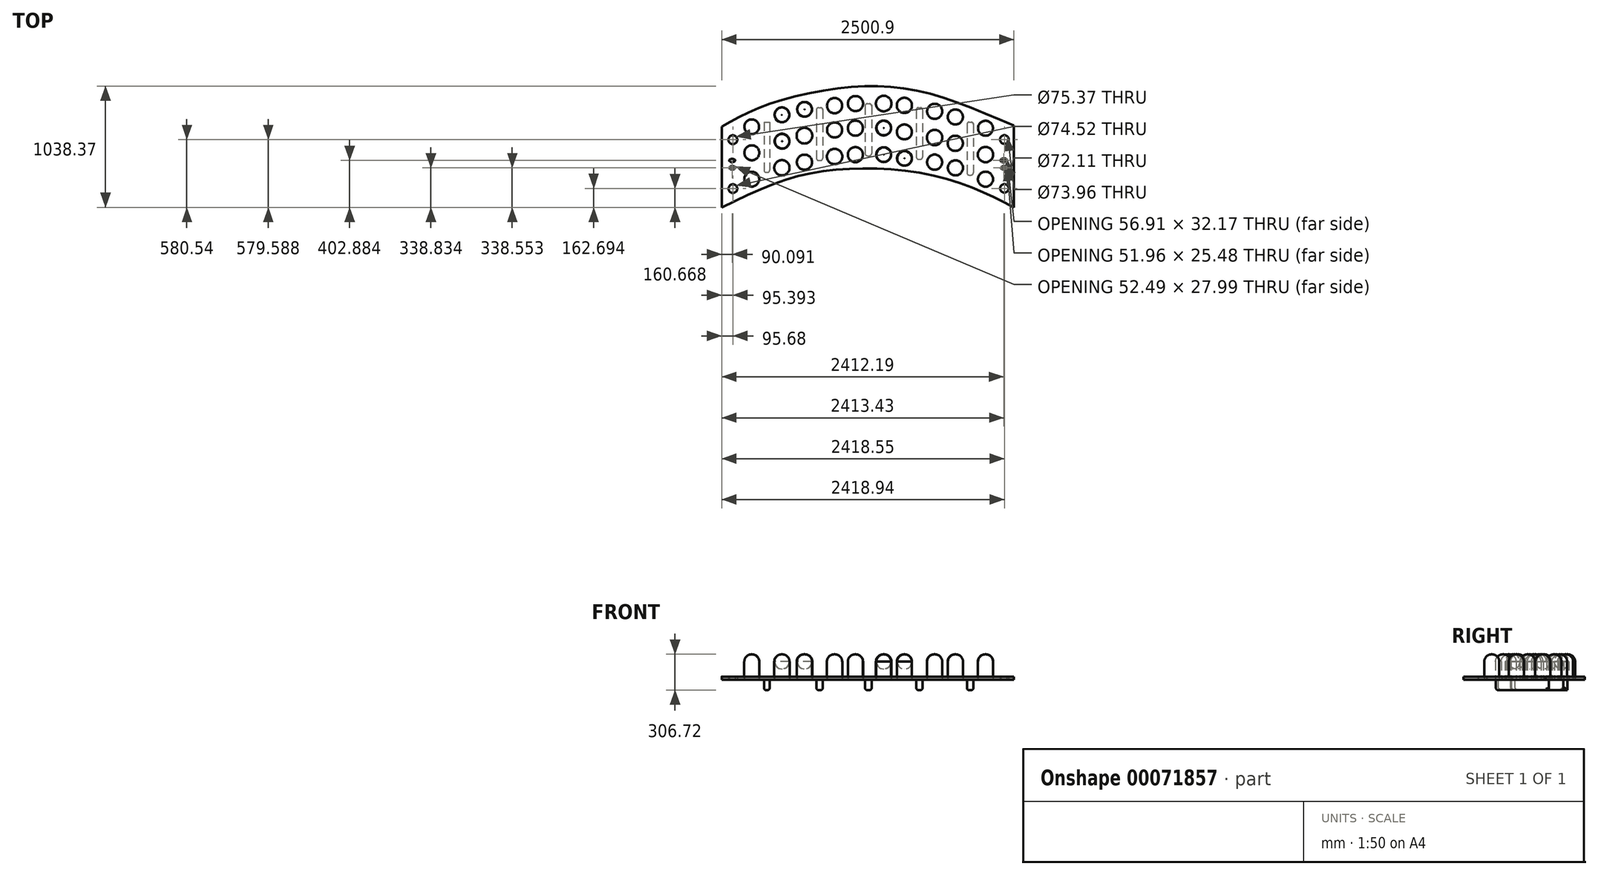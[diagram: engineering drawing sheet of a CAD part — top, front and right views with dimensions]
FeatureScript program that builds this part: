
annotation { "Feature Type Name" : "Feature", "Feature Type Description" : "" }
export const myFeature = defineFeature(function(context is Context, id is Id, definition is map)
    precondition{}
    {
        {
            var Q0;
            Q0=qCreatedBy(makeId("Top.planeOp"),FACE);
            var sketch = newSketch(context, id + "F0", { "sketchPlane" : qUnion([Q0])});
            skCircle(sketch, "E0", {"center": v(-1121.67, 314.92) * mm, "radius": 37.68 * mm});
            skArc(sketch, "E1", {"start": v(-1009.36, 266.44) * mm, "mid": v(-958.88, 121.92) * mm, "end": v(-910.93, 267.3) * mm});
            skFitSpline(sketch, "E2", {"points": [v(-1009.36, 266.44) * mm, v(-910.93, 267.3) * mm], "startDerivative": vector(98.35, 0.86) * mm, "endDerivative": vector(98.35, 0.86) * mm});
            skCircle(sketch, "E3", {"center": v(-959.59, 202.75) * mm, "radius": 63.82 * mm});
            skCircle(sketch, "E4", {"center": v(-1121.38, -104) * mm, "radius": 37.26 * mm});
            skCircle(sketch, "E5", {"center": v(1201.49, -101.98) * mm, "radius": 36.06 * mm});
            skCircle(sketch, "E6", {"center": v(1201.88, 315.87) * mm, "radius": 36.98 * mm});
            skCircle(sketch, "E7", {"center": v(1040.12, -23.25) * mm, "radius": 64.34 * mm});
            skArc(sketch, "E8", {"start": v(996.77, 45.5) * mm, "mid": v(1039.5, -104.53) * mm, "end": v(1084.49, 44.85) * mm});
            skArc(sketch, "E9", {"start": v(1084.6, 118.34) * mm, "mid": v(1039.83, 269.47) * mm, "end": v(996.09, 118.03) * mm});
            skCircle(sketch, "E10", {"center": v(1040.1, 187.36) * mm, "radius": 65.52 * mm});
            skCircle(sketch, "E11", {"center": v(782.85, 73.45) * mm, "radius": 64.5 * mm});
            skArc(sketch, "E12", {"start": v(739.54, 141.2) * mm, "mid": v(783.11, -6.96) * mm, "end": v(825.71, 141.49) * mm});
            skCircle(sketch, "E13", {"center": v(604.63, 122.55) * mm, "radius": 64.82 * mm});
            skArc(sketch, "E14", {"start": v(562.8, 190.06) * mm, "mid": v(605.03, 43.13) * mm, "end": v(645.78, 190.48) * mm});
            skCircle(sketch, "E15", {"center": v(781.42, 283.68) * mm, "radius": 65 * mm});
            skArc(sketch, "E16", {"start": v(735.27, 351.66) * mm, "mid": v(781.19, 201.51) * mm, "end": v(827.98, 351.39) * mm});
            skCircle(sketch, "E17", {"center": v(1040.05, 412.9) * mm, "radius": 64.08 * mm});
            skArc(sketch, "E18", {"start": v(1082.73, 344.5) * mm, "mid": v(1040.14, 493.54) * mm, "end": v(997.22, 344.6) * mm});
            skCircle(sketch, "E19", {"center": v(781.81, 509.34) * mm, "radius": 64.52 * mm});
            skArc(sketch, "E20", {"start": v(826.57, 440.73) * mm, "mid": v(781.74, 591.27) * mm, "end": v(737.18, 440.65) * mm});
            skCircle(sketch, "E21", {"center": v(605.1, 557.46) * mm, "radius": 64.57 * mm});
            skArc(sketch, "E22", {"start": v(646.48, 489.26) * mm, "mid": v(604.55, 637.22) * mm, "end": v(564.68, 488.7) * mm});
            skCircle(sketch, "E23", {"center": v(604.23, 332.64) * mm, "radius": 65.8 * mm});
            skArc(sketch, "E24", {"start": v(642.2, 263.79) * mm, "mid": v(602.61, 413.33) * mm, "end": v(565.81, 263.08) * mm});
            skCircle(sketch, "E25", {"center": v(345.86, 608.12) * mm, "radius": 64.94 * mm});
            skCircle(sketch, "E26", {"center": v(169, 623.72) * mm, "radius": 66.59 * mm});
            skArc(sketch, "E27", {"start": v(211.25, 553.01) * mm, "mid": v(169.2, 706.09) * mm, "end": v(126.42, 553.22) * mm});
            skArc(sketch, "E28", {"start": v(392.18, 538) * mm, "mid": v(344.45, 692.14) * mm, "end": v(301.92, 536.48) * mm});
            skCircle(sketch, "E29", {"center": v(345.86, 381.33) * mm, "radius": 63.88 * mm});
            skArc(sketch, "E30", {"start": v(300.08, 449.99) * mm, "mid": v(345.37, 298.81) * mm, "end": v(392.45, 449.44) * mm});
            skCircle(sketch, "E31", {"center": v(169, 414.62) * mm, "radius": 63.6 * mm});
            skArc(sketch, "E32", {"start": v(210.1, 344.64) * mm, "mid": v(168.9, 495.77) * mm, "end": v(128.1, 344.53) * mm});
            skCircle(sketch, "E33", {"center": v(169, 186.8) * mm, "radius": 63.46 * mm});
            skArc(sketch, "E34", {"start": v(126.98, 255.02) * mm, "mid": v(168.76, 106.66) * mm, "end": v(211.44, 254.76) * mm});
            skCircle(sketch, "E35", {"center": v(346.9, 155.58) * mm, "radius": 63.46 * mm});
            skArc(sketch, "E36", {"start": v(299.4, 224.7) * mm, "mid": v(345.11, 74.2) * mm, "end": v(393.54, 223.85) * mm});
            skCircle(sketch, "E37", {"center": v(-72.35, 623.72) * mm, "radius": 64.8 * mm});
            skArc(sketch, "E38", {"start": v(-31.79, 552.97) * mm, "mid": v(-71.26, 705.26) * mm, "end": v(-114.78, 554.08) * mm});
            skCircle(sketch, "E39", {"center": v(-251.28, 606.04) * mm, "radius": 65.03 * mm});
            skArc(sketch, "E40", {"start": v(-206.16, 538) * mm, "mid": v(-251.6, 689.58) * mm, "end": v(-295.85, 537.65) * mm});
            skCircle(sketch, "E41", {"center": v(-73.39, 413.58) * mm, "radius": 64.63 * mm});
            skArc(sketch, "E42", {"start": v(-117.78, 482.86) * mm, "mid": v(-73.02, 331.3) * mm, "end": v(-29.61, 483.26) * mm});
            skCircle(sketch, "E43", {"center": v(-251.28, 397.98) * mm, "radius": 64.7 * mm});
            skArc(sketch, "E44", {"start": v(-209.8, 327.74) * mm, "mid": v(-251.54, 479.54) * mm, "end": v(-292.3, 327.48) * mm});
            skCircle(sketch, "E45", {"center": v(-73.52, 186.84) * mm, "radius": 64.82 * mm});
            skArc(sketch, "E46", {"start": v(-113.86, 256.24) * mm, "mid": v(-72.98, 106.57) * mm, "end": v(-34.13, 256.78) * mm});
            skCircle(sketch, "E47", {"center": v(-251.54, 170.66) * mm, "radius": 65.86 * mm});
            skArc(sketch, "E48", {"start": v(-294.03, 239.99) * mm, "mid": v(-251.39, 89.35) * mm, "end": v(-209.32, 240.15) * mm});
            skCircle(sketch, "E49", {"center": v(-508.16, 574.52) * mm, "radius": 63.15 * mm});
            skArc(sketch, "E50", {"start": v(-459.73, 508.88) * mm, "mid": v(-509.28, 656.09) * mm, "end": v(-554.77, 507.58) * mm});
            skCircle(sketch, "E51", {"center": v(-509.33, 349.16) * mm, "radius": 67.21 * mm});
            skArc(sketch, "E52", {"start": v(-550.67, 417.2) * mm, "mid": v(-508.63, 269.54) * mm, "end": v(-469.18, 417.91) * mm});
            skCircle(sketch, "E53", {"center": v(-702, 527.82) * mm, "radius": 63.06 * mm});
            skArc(sketch, "E54", {"start": v(-653.72, 461.86) * mm, "mid": v(-702.05, 609.55) * mm, "end": v(-750.2, 461.8) * mm});
            skCircle(sketch, "E55", {"center": v(-700.83, 301.28) * mm, "radius": 63.74 * mm});
            skArc(sketch, "E56", {"start": v(-662.8, 232.28) * mm, "mid": v(-700.48, 380.06) * mm, "end": v(-739.47, 232.63) * mm});
            skCircle(sketch, "E57", {"center": v(-508.93, 122.36) * mm, "radius": 64.67 * mm});
            skArc(sketch, "E58", {"start": v(-554.53, 190.63) * mm, "mid": v(-508.86, 40.26) * mm, "end": v(-463.45, 190.7) * mm});
            skCircle(sketch, "E59", {"center": v(-702.18, 74.48) * mm, "radius": 65.4 * mm});
            skArc(sketch, "E60", {"start": v(-745.47, 142.47) * mm, "mid": v(-702.86, -6.12) * mm, "end": v(-657.77, 141.74) * mm});
            skCircle(sketch, "E61", {"center": v(-960.27, 425.7) * mm, "radius": 62.75 * mm});
            skArc(sketch, "E62", {"start": v(-914.27, 360.84) * mm, "mid": v(-957.9, 507.67) * mm, "end": v(-1003.02, 361.3) * mm});
            skCircle(sketch, "E63", {"center": v(-960.27, -23.05) * mm, "radius": 64.01 * mm});
            skArc(sketch, "E64", {"start": v(-1009.36, 44.48) * mm, "mid": v(-962.23, -105.4) * mm, "end": v(-915.1, 44.48) * mm});
            skFitSpline(sketch, "E65", {"points": [v(-1003.02, 361.3) * mm, v(-914.27, 360.84) * mm], "startDerivative": vector(88.69, -0.44) * mm, "endDerivative": vector(88.69, -0.44) * mm});
            skFitSpline(sketch, "E66", {"points": [v(-1009.36, 44.48) * mm, v(-915.1, 44.48) * mm], "startDerivative": vector(94.27, 0) * mm, "endDerivative": vector(94.27, 0) * mm});
            skFitSpline(sketch, "E67", {"points": [v(-745.47, 142.47) * mm, v(-657.77, 141.74) * mm], "startDerivative": vector(87.63, -0.72) * mm, "endDerivative": vector(87.63, -0.72) * mm});
            skFitSpline(sketch, "E68", {"points": [v(-739.47, 232.63) * mm, v(-662.8, 232.28) * mm], "startDerivative": vector(76.67, -0.26) * mm, "endDerivative": vector(76.67, -0.26) * mm});
            skFitSpline(sketch, "E69", {"points": [v(-750.2, 461.8) * mm, v(-653.72, 461.86) * mm], "startDerivative": vector(96.42, 0.06) * mm, "endDerivative": vector(96.42, 0.06) * mm});
            skFitSpline(sketch, "E70", {"points": [v(-554.53, 190.63) * mm, v(-463.45, 190.7) * mm], "startDerivative": vector(91.01, 0.07) * mm, "endDerivative": vector(91.01, 0.07) * mm});
            skFitSpline(sketch, "E71", {"points": [v(-550.67, 417.2) * mm, v(-469.18, 417.91) * mm], "startDerivative": vector(81.45, 0.75) * mm, "endDerivative": vector(81.45, 0.75) * mm});
            skFitSpline(sketch, "E72", {"points": [v(-554.77, 507.58) * mm, v(-459.73, 508.88) * mm], "startDerivative": vector(95, 1.36) * mm, "endDerivative": vector(95, 1.36) * mm});
            skFitSpline(sketch, "E73", {"points": [v(-295.85, 537.65) * mm, v(-206.16, 538) * mm], "startDerivative": vector(89.6, 0.34) * mm, "endDerivative": vector(89.6, 0.34) * mm});
            skFitSpline(sketch, "E74", {"points": [v(-292.3, 327.48) * mm, v(-209.8, 327.74) * mm], "startDerivative": vector(82.52, 0.22) * mm, "endDerivative": vector(82.52, 0.22) * mm});
            skFitSpline(sketch, "E75", {"points": [v(-294.03, 239.99) * mm, v(-209.32, 240.15) * mm], "startDerivative": vector(84.65, 0.17) * mm, "endDerivative": vector(84.65, 0.17) * mm});
            skFitSpline(sketch, "E76", {"points": [v(-31.79, 552.97) * mm, v(-114.78, 554.08) * mm], "startDerivative": vector(-82.96, 1.17) * mm, "endDerivative": vector(-82.96, 1.17) * mm});
            skFitSpline(sketch, "E77", {"points": [v(-29.61, 483.26) * mm, v(-117.78, 482.86) * mm], "startDerivative": vector(-88.09, -0.4) * mm, "endDerivative": vector(-88.09, -0.4) * mm});
            skFitSpline(sketch, "E78", {"points": [v(-34.13, 256.78) * mm, v(-113.86, 256.24) * mm], "startDerivative": vector(-79.72, -0.52) * mm, "endDerivative": vector(-79.72, -0.52) * mm});
            skFitSpline(sketch, "E79", {"points": [v(126.42, 553.22) * mm, v(211.25, 553.01) * mm], "startDerivative": vector(84.78, -0.22) * mm, "endDerivative": vector(84.78, -0.22) * mm});
            skFitSpline(sketch, "E80", {"points": [v(301.92, 536.48) * mm, v(392.18, 538) * mm], "startDerivative": vector(90.18, 1.52) * mm, "endDerivative": vector(90.18, 1.52) * mm});
            skFitSpline(sketch, "E81", {"points": [v(300.08, 449.99) * mm, v(392.45, 449.44) * mm], "startDerivative": vector(92.32, -0.53) * mm, "endDerivative": vector(92.32, -0.53) * mm});
            skFitSpline(sketch, "E82", {"points": [v(210.1, 344.64) * mm, v(128.1, 344.53) * mm], "startDerivative": vector(-81.99, -0.14) * mm, "endDerivative": vector(-81.99, -0.14) * mm});
            skFitSpline(sketch, "E83", {"points": [v(126.98, 255.02) * mm, v(211.44, 254.76) * mm], "startDerivative": vector(84.39, -0.26) * mm, "endDerivative": vector(84.39, -0.26) * mm});
            skFitSpline(sketch, "E84", {"points": [v(299.4, 224.7) * mm, v(393.54, 223.85) * mm], "startDerivative": vector(94.13, -0.8) * mm, "endDerivative": vector(94.13, -0.8) * mm});
            skFitSpline(sketch, "E85", {"points": [v(564.68, 488.7) * mm, v(646.48, 489.26) * mm], "startDerivative": vector(81.76, 0.6) * mm, "endDerivative": vector(81.76, 0.6) * mm});
            skFitSpline(sketch, "E86", {"points": [v(737.18, 440.65) * mm, v(826.57, 440.73) * mm], "startDerivative": vector(89.3, 0.08) * mm, "endDerivative": vector(89.3, 0.08) * mm});
            skFitSpline(sketch, "E87", {"points": [v(735.27, 351.66) * mm, v(827.98, 351.39) * mm], "startDerivative": vector(92.7, -0.2) * mm, "endDerivative": vector(92.7, -0.2) * mm});
            skFitSpline(sketch, "E88", {"points": [v(565.81, 263.08) * mm, v(642.2, 263.79) * mm], "startDerivative": vector(76.34, 0.69) * mm, "endDerivative": vector(76.34, 0.69) * mm});
            skFitSpline(sketch, "E89", {"points": [v(562.8, 190.06) * mm, v(645.78, 190.48) * mm], "startDerivative": vector(82.93, 0.43) * mm, "endDerivative": vector(82.93, 0.43) * mm});
            skFitSpline(sketch, "E90", {"points": [v(825.71, 141.49) * mm, v(739.54, 141.2) * mm], "startDerivative": vector(-86.1, -0.28) * mm, "endDerivative": vector(-86.1, -0.28) * mm});
            skFitSpline(sketch, "E91", {"points": [v(997.22, 344.6) * mm, v(1082.73, 344.5) * mm], "startDerivative": vector(85.43, -0.1) * mm, "endDerivative": vector(85.43, -0.1) * mm});
            skFitSpline(sketch, "E92", {"points": [v(996.09, 118.03) * mm, v(1084.6, 118.34) * mm], "startDerivative": vector(88.43, 0.3) * mm, "endDerivative": vector(88.43, 0.3) * mm});
            skFitSpline(sketch, "E93", {"points": [v(996.77, 45.5) * mm, v(1084.49, 44.85) * mm], "startDerivative": vector(87.64, -0.65) * mm, "endDerivative": vector(87.64, -0.65) * mm});
            skLineSegment(sketch, "E94.bottom", {"start": v(-855.95, 463.96) * mm, "end": v(-806.83, 463.96) * mm});
            skLineSegment(sketch, "E94.top", {"start": v(-855.95, 34.85) * mm, "end": v(-806.83, 34.85) * mm});
            skLineSegment(sketch, "E94.left", {"start": v(-855.95, 463.96) * mm, "end": v(-855.95, 34.85) * mm});
            skLineSegment(sketch, "E94.right", {"start": v(-806.83, 463.96) * mm, "end": v(-806.83, 34.85) * mm});
            skLineSegment(sketch, "E95.bottom", {"start": v(-407.37, 589.08) * mm, "end": v(-352.7, 589.08) * mm});
            skLineSegment(sketch, "E95.top", {"start": v(-407.37, 136.8) * mm, "end": v(-352.7, 136.8) * mm});
            skLineSegment(sketch, "E95.left", {"start": v(-407.37, 589.08) * mm, "end": v(-407.37, 136.8) * mm});
            skLineSegment(sketch, "E95.right", {"start": v(-352.7, 589.08) * mm, "end": v(-352.7, 136.8) * mm});
            skLineSegment(sketch, "E96.bottom", {"start": v(9.2, 622.77) * mm, "end": v(65.98, 622.77) * mm});
            skLineSegment(sketch, "E96.top", {"start": v(9.2, 177.29) * mm, "end": v(65.98, 177.29) * mm});
            skLineSegment(sketch, "E96.left", {"start": v(9.2, 622.77) * mm, "end": v(9.2, 177.29) * mm});
            skLineSegment(sketch, "E96.right", {"start": v(65.98, 622.77) * mm, "end": v(65.98, 177.29) * mm});
            skLineSegment(sketch, "E97.bottom", {"start": v(447.86, 589.71) * mm, "end": v(502.02, 589.71) * mm});
            skLineSegment(sketch, "E97.top", {"start": v(447.86, 146.74) * mm, "end": v(502.02, 146.74) * mm});
            skLineSegment(sketch, "E97.left", {"start": v(447.86, 589.71) * mm, "end": v(447.86, 146.74) * mm});
            skLineSegment(sketch, "E97.right", {"start": v(502.02, 589.71) * mm, "end": v(502.02, 146.74) * mm});
            skLineSegment(sketch, "E98.bottom", {"start": v(880.9, 464.82) * mm, "end": v(936.57, 464.82) * mm});
            skLineSegment(sketch, "E98.top", {"start": v(880.9, 12.03) * mm, "end": v(936.57, 12.03) * mm});
            skLineSegment(sketch, "E98.left", {"start": v(880.9, 464.82) * mm, "end": v(880.9, 12.03) * mm});
            skLineSegment(sketch, "E98.right", {"start": v(936.57, 464.82) * mm, "end": v(936.57, 12.03) * mm});
            skEllipse(sketch, "E99", {"center": v(1195.13, 138.21) * mm, "majorRadius": 28.45 * mm, "minorRadius": 16.08 * mm, "majorAxis": v(1, 0)});
            skEllipse(sketch, "E100", {"center": v(1196.37, 73.88) * mm, "majorRadius": 25.98 * mm, "minorRadius": 12.74 * mm, "majorAxis": v(1, 0)});
            skEllipse(sketch, "E101", {"center": v(-1127.84, 137.15) * mm, "majorRadius": 24.5 * mm, "minorRadius": 14.14 * mm, "majorAxis": v(-1, 0)});
            skEllipse(sketch, "E102", {"center": v(-1126.97, 74.16) * mm, "majorRadius": 26.24 * mm, "minorRadius": 14 * mm, "majorAxis": v(1, 0)});
            skFitSpline(sketch, "E103", {"points": [v(-1217.06, 426.7) * mm, v(-1216.3, -264.67) * mm], "startDerivative": vector(0, -694.41) * mm, "endDerivative": vector(0, -694.41) * mm});
            skFitSpline(sketch, "E104", {"points": [v(1283.84, -264.67) * mm, v(1283.84, 435.53) * mm], "startDerivative": vector(0, 703.24) * mm, "endDerivative": vector(0, 703.24) * mm});
            skPoint(sketch, "E105.3.internal.snap0", {"position": v(-702.05, 609.55) * mm});
            skFitSpline(sketch, "E105", {"points": [v(1283.84, 435.53) * mm, v(501.33, 723.9) * mm, v(-146, 762.14) * mm, v(-840.42, 609.55) * mm, v(-1217.06, 426.7) * mm], "startDerivative": vector(-2819.24, 1209.08) * mm, "endDerivative": vector(-1679, -949.55) * mm});
            skPoint(sketch, "E106.2.internal.snap0", {"position": v(-1126.97, 60.17) * mm});
            skFitSpline(sketch, "E106", {"points": [v(-1216.3, -264.67) * mm, v(-682.25, -32.14) * mm, v(-202.55, 60.17) * mm, v(371.33, 48.06) * mm, v(916.46, -90.83) * mm, v(1283.84, -264.67) * mm], "startDerivative": vector(2555.4, 1244.06) * mm, "endDerivative": vector(1956.51, -1028.42) * mm});
            skSolve(sketch);
        }
        {
            var Q0;
            Q0=makeQuery(id+"F0.imprint","IMPRINT",FACE,{"disambiguationData":[TD([[makeQuery(id+"F0.imprint","IMPRINT",EDGE,{"derivedFrom":sQuery(id+"F0.wireOp",EDGE,"E63")}),1.0]])]});
            var Q1;
            Q1=makeQuery(id+"F0.imprint","IMPRINT",FACE,{"disambiguationData":[TD([[makeQuery(id+"F0.imprint","IMPRINT",EDGE,{"derivedFrom":sQuery(id+"F0.wireOp",EDGE,"E3")}),1.0]])]});
            var Q2;
            Q2=makeQuery(id+"F0.imprint","IMPRINT",FACE,{"disambiguationData":[TD([[makeQuery(id+"F0.imprint","IMPRINT",EDGE,{"derivedFrom":sQuery(id+"F0.wireOp",EDGE,"E61")}),1.0]])]});
            var Q3;
            Q3=makeQuery(id+"F0.imprint","IMPRINT",FACE,{"disambiguationData":[TD([[makeQuery(id+"F0.imprint","IMPRINT",EDGE,{"derivedFrom":sQuery(id+"F0.wireOp",EDGE,"E53")}),1.0]])]});
            var Q4;
            Q4=makeQuery(id+"F0.imprint","IMPRINT",FACE,{"disambiguationData":[TD([[makeQuery(id+"F0.imprint","IMPRINT",EDGE,{"derivedFrom":sQuery(id+"F0.wireOp",EDGE,"E49")}),1.0]])]});
            var Q5;
            Q5=makeQuery(id+"F0.imprint","IMPRINT",FACE,{"disambiguationData":[TD([[makeQuery(id+"F0.imprint","IMPRINT",EDGE,{"derivedFrom":sQuery(id+"F0.wireOp",EDGE,"E55")}),1.0]])]});
            var Q6;
            Q6=makeQuery(id+"F0.imprint","IMPRINT",FACE,{"disambiguationData":[TD([[makeQuery(id+"F0.imprint","IMPRINT",EDGE,{"derivedFrom":sQuery(id+"F0.wireOp",EDGE,"E51")}),1.0]])]});
            var Q7;
            Q7=makeQuery(id+"F0.imprint","IMPRINT",FACE,{"disambiguationData":[TD([[makeQuery(id+"F0.imprint","IMPRINT",EDGE,{"derivedFrom":sQuery(id+"F0.wireOp",EDGE,"E59")}),1.0]])]});
            var Q8;
            Q8=makeQuery(id+"F0.imprint","IMPRINT",FACE,{"disambiguationData":[TD([[makeQuery(id+"F0.imprint","IMPRINT",EDGE,{"derivedFrom":sQuery(id+"F0.wireOp",EDGE,"E57")}),1.0]])]});
            var Q9;
            Q9=makeQuery(id+"F0.imprint","IMPRINT",FACE,{"disambiguationData":[TD([[makeQuery(id+"F0.imprint","IMPRINT",EDGE,{"derivedFrom":sQuery(id+"F0.wireOp",EDGE,"E47")}),1.0]])]});
            var Q10;
            Q10=makeQuery(id+"F0.imprint","IMPRINT",FACE,{"disambiguationData":[TD([[makeQuery(id+"F0.imprint","IMPRINT",EDGE,{"derivedFrom":sQuery(id+"F0.wireOp",EDGE,"E43")}),1.0]])]});
            var Q11;
            Q11=makeQuery(id+"F0.imprint","IMPRINT",FACE,{"disambiguationData":[TD([[makeQuery(id+"F0.imprint","IMPRINT",EDGE,{"derivedFrom":sQuery(id+"F0.wireOp",EDGE,"E39")}),1.0]])]});
            var Q12;
            Q12=makeQuery(id+"F0.imprint","IMPRINT",FACE,{"disambiguationData":[TD([[makeQuery(id+"F0.imprint","IMPRINT",EDGE,{"derivedFrom":sQuery(id+"F0.wireOp",EDGE,"E37")}),1.0]])]});
            var Q13;
            Q13=makeQuery(id+"F0.imprint","IMPRINT",FACE,{"disambiguationData":[TD([[makeQuery(id+"F0.imprint","IMPRINT",EDGE,{"derivedFrom":sQuery(id+"F0.wireOp",EDGE,"E41")}),1.0]])]});
            var Q14;
            Q14=makeQuery(id+"F0.imprint","IMPRINT",FACE,{"disambiguationData":[TD([[makeQuery(id+"F0.imprint","IMPRINT",EDGE,{"derivedFrom":sQuery(id+"F0.wireOp",EDGE,"E45")}),1.0]])]});
            var Q15;
            Q15=makeQuery(id+"F0.imprint","IMPRINT",FACE,{"disambiguationData":[TD([[makeQuery(id+"F0.imprint","IMPRINT",EDGE,{"derivedFrom":sQuery(id+"F0.wireOp",EDGE,"E33")}),1.0]])]});
            var Q16;
            Q16=makeQuery(id+"F0.imprint","IMPRINT",FACE,{"disambiguationData":[TD([[makeQuery(id+"F0.imprint","IMPRINT",EDGE,{"derivedFrom":sQuery(id+"F0.wireOp",EDGE,"E31")}),1.0]])]});
            var Q17;
            Q17=makeQuery(id+"F0.imprint","IMPRINT",FACE,{"disambiguationData":[TD([[makeQuery(id+"F0.imprint","IMPRINT",EDGE,{"derivedFrom":sQuery(id+"F0.wireOp",EDGE,"E26")}),1.0]])]});
            var Q18;
            Q18=makeQuery(id+"F0.imprint","IMPRINT",FACE,{"disambiguationData":[TD([[makeQuery(id+"F0.imprint","IMPRINT",EDGE,{"derivedFrom":sQuery(id+"F0.wireOp",EDGE,"E25")}),1.0]])]});
            var Q19;
            Q19=makeQuery(id+"F0.imprint","IMPRINT",FACE,{"disambiguationData":[TD([[makeQuery(id+"F0.imprint","IMPRINT",EDGE,{"derivedFrom":sQuery(id+"F0.wireOp",EDGE,"E29")}),1.0]])]});
            var Q20;
            Q20=makeQuery(id+"F0.imprint","IMPRINT",FACE,{"disambiguationData":[TD([[makeQuery(id+"F0.imprint","IMPRINT",EDGE,{"derivedFrom":sQuery(id+"F0.wireOp",EDGE,"E35")}),1.0]])]});
            var Q21;
            Q21=makeQuery(id+"F0.imprint","IMPRINT",FACE,{"disambiguationData":[TD([[makeQuery(id+"F0.imprint","IMPRINT",EDGE,{"derivedFrom":sQuery(id+"F0.wireOp",EDGE,"E23")}),1.0]])]});
            var Q22;
            Q22=makeQuery(id+"F0.imprint","IMPRINT",FACE,{"disambiguationData":[TD([[makeQuery(id+"F0.imprint","IMPRINT",EDGE,{"derivedFrom":sQuery(id+"F0.wireOp",EDGE,"E21")}),1.0]])]});
            var Q23;
            Q23=makeQuery(id+"F0.imprint","IMPRINT",FACE,{"disambiguationData":[TD([[makeQuery(id+"F0.imprint","IMPRINT",EDGE,{"derivedFrom":sQuery(id+"F0.wireOp",EDGE,"E19")}),1.0]])]});
            var Q24;
            Q24=makeQuery(id+"F0.imprint","IMPRINT",FACE,{"disambiguationData":[TD([[makeQuery(id+"F0.imprint","IMPRINT",EDGE,{"derivedFrom":sQuery(id+"F0.wireOp",EDGE,"E15")}),1.0]])]});
            var Q25;
            Q25=makeQuery(id+"F0.imprint","IMPRINT",FACE,{"disambiguationData":[TD([[makeQuery(id+"F0.imprint","IMPRINT",EDGE,{"derivedFrom":sQuery(id+"F0.wireOp",EDGE,"E13")}),1.0]])]});
            var Q26;
            Q26=makeQuery(id+"F0.imprint","IMPRINT",FACE,{"disambiguationData":[TD([[makeQuery(id+"F0.imprint","IMPRINT",EDGE,{"derivedFrom":sQuery(id+"F0.wireOp",EDGE,"E11")}),1.0]])]});
            var Q27;
            Q27=makeQuery(id+"F0.imprint","IMPRINT",FACE,{"disambiguationData":[TD([[makeQuery(id+"F0.imprint","IMPRINT",EDGE,{"derivedFrom":sQuery(id+"F0.wireOp",EDGE,"E7")}),1.0]])]});
            var Q28;
            Q28=makeQuery(id+"F0.imprint","IMPRINT",FACE,{"disambiguationData":[TD([[makeQuery(id+"F0.imprint","IMPRINT",EDGE,{"derivedFrom":sQuery(id+"F0.wireOp",EDGE,"E10")}),1.0]])]});
            var Q29;
            Q29=makeQuery(id+"F0.imprint","IMPRINT",FACE,{"disambiguationData":[TD([[makeQuery(id+"F0.imprint","IMPRINT",EDGE,{"derivedFrom":sQuery(id+"F0.wireOp",EDGE,"E17")}),1.0]])]});
            extrude(context, id + "F1", {"entities" : qUnion([Q0, Q1, Q2, Q3, Q4, Q5, Q6, Q7, Q8, Q9, Q10, Q11, Q12, Q13, Q14, Q15, Q16, Q17, Q18, Q19, Q20, Q21, Q22, Q23, Q24, Q25, Q26, Q27, Q28, Q29]), "depth" : 216.72 * mm});
        }
        {
            var Q0;
            Q0=makeQuery(id+"F0.imprint","IMPRINT",FACE,{"disambiguationData":[TD([[makeQuery(id+"F0.imprint","IMPRINT",EDGE,{"derivedFrom":sQuery(id+"F0.wireOp",EDGE,"E0")}),-1.0]])]});
            var Q1;
            Q1=makeQuery(id+"F0.imprint","IMPRINT",FACE,{"disambiguationData":[TD([[makeQuery(id+"F0.imprint","IMPRINT",EDGE,{"derivedFrom":sQuery(id+"F0.wireOp",EDGE,"E3")}),1.0]])]});
            var Q2;
            Q2=makeQuery(id+"F0.imprint","IMPRINT",FACE,{"disambiguationData":[TD([[makeQuery(id+"F0.imprint","IMPRINT",EDGE,{"derivedFrom":sQuery(id+"F0.wireOp",EDGE,"E1")}),1.0]])]});
            var Q3;
            Q3=makeQuery(id+"F0.imprint","IMPRINT",FACE,{"disambiguationData":[TD([[makeQuery(id+"F0.imprint","IMPRINT",EDGE,{"derivedFrom":sQuery(id+"F0.wireOp",EDGE,"E63")}),1.0]])]});
            var Q4;
            Q4=makeQuery(id+"F0.imprint","IMPRINT",FACE,{"disambiguationData":[TD([[makeQuery(id+"F0.imprint","IMPRINT",EDGE,{"derivedFrom":sQuery(id+"F0.wireOp",EDGE,"E63")}),-1.0]])]});
            var Q5;
            Q5=makeQuery(id+"F0.imprint","IMPRINT",FACE,{"disambiguationData":[TD([[makeQuery(id+"F0.imprint","IMPRINT",EDGE,{"derivedFrom":sQuery(id+"F0.wireOp",EDGE,"E59")}),1.0]])]});
            var Q6;
            Q6=makeQuery(id+"F0.imprint","IMPRINT",FACE,{"disambiguationData":[TD([[makeQuery(id+"F0.imprint","IMPRINT",EDGE,{"derivedFrom":sQuery(id+"F0.wireOp",EDGE,"E59")}),-1.0]])]});
            var Q7;
            Q7=makeQuery(id+"F0.imprint","IMPRINT",FACE,{"disambiguationData":[TD([[makeQuery(id+"F0.imprint","IMPRINT",EDGE,{"derivedFrom":sQuery(id+"F0.wireOp",EDGE,"E57")}),1.0]])]});
            var Q8;
            Q8=makeQuery(id+"F0.imprint","IMPRINT",FACE,{"disambiguationData":[TD([[makeQuery(id+"F0.imprint","IMPRINT",EDGE,{"derivedFrom":sQuery(id+"F0.wireOp",EDGE,"E57")}),-1.0]])]});
            var Q9;
            Q9=makeQuery(id+"F0.imprint","IMPRINT",FACE,{"disambiguationData":[TD([[makeQuery(id+"F0.imprint","IMPRINT",EDGE,{"derivedFrom":sQuery(id+"F0.wireOp",EDGE,"E55")}),1.0]])]});
            var Q10;
            Q10=makeQuery(id+"F0.imprint","IMPRINT",FACE,{"disambiguationData":[TD([[makeQuery(id+"F0.imprint","IMPRINT",EDGE,{"derivedFrom":sQuery(id+"F0.wireOp",EDGE,"E55")}),-1.0]])]});
            var Q11;
            Q11=makeQuery(id+"F0.imprint","IMPRINT",FACE,{"disambiguationData":[TD([[makeQuery(id+"F0.imprint","IMPRINT",EDGE,{"derivedFrom":sQuery(id+"F0.wireOp",EDGE,"E51")}),-1.0]])]});
            var Q12;
            Q12=makeQuery(id+"F0.imprint","IMPRINT",FACE,{"disambiguationData":[TD([[makeQuery(id+"F0.imprint","IMPRINT",EDGE,{"derivedFrom":sQuery(id+"F0.wireOp",EDGE,"E51")}),1.0]])]});
            var Q13;
            Q13=makeQuery(id+"F0.imprint","IMPRINT",FACE,{"disambiguationData":[TD([[makeQuery(id+"F0.imprint","IMPRINT",EDGE,{"derivedFrom":sQuery(id+"F0.wireOp",EDGE,"E49")}),-1.0]])]});
            var Q14;
            Q14=makeQuery(id+"F0.imprint","IMPRINT",FACE,{"disambiguationData":[TD([[makeQuery(id+"F0.imprint","IMPRINT",EDGE,{"derivedFrom":sQuery(id+"F0.wireOp",EDGE,"E49")}),1.0]])]});
            var Q15;
            Q15=makeQuery(id+"F0.imprint","IMPRINT",FACE,{"disambiguationData":[TD([[makeQuery(id+"F0.imprint","IMPRINT",EDGE,{"derivedFrom":sQuery(id+"F0.wireOp",EDGE,"E53")}),-1.0]])]});
            var Q16;
            Q16=makeQuery(id+"F0.imprint","IMPRINT",FACE,{"disambiguationData":[TD([[makeQuery(id+"F0.imprint","IMPRINT",EDGE,{"derivedFrom":sQuery(id+"F0.wireOp",EDGE,"E53")}),1.0]])]});
            var Q17;
            Q17=makeQuery(id+"F0.imprint","IMPRINT",FACE,{"disambiguationData":[TD([[makeQuery(id+"F0.imprint","IMPRINT",EDGE,{"derivedFrom":sQuery(id+"F0.wireOp",EDGE,"E61")}),-1.0]])]});
            var Q18;
            Q18=makeQuery(id+"F0.imprint","IMPRINT",FACE,{"disambiguationData":[TD([[makeQuery(id+"F0.imprint","IMPRINT",EDGE,{"derivedFrom":sQuery(id+"F0.wireOp",EDGE,"E61")}),1.0]])]});
            var Q19;
            Q19=makeQuery(id+"F0.imprint","IMPRINT",FACE,{"disambiguationData":[TD([[makeQuery(id+"F0.imprint","IMPRINT",EDGE,{"derivedFrom":sQuery(id+"F0.wireOp",EDGE,"E43")}),-1.0]])]});
            var Q20;
            Q20=makeQuery(id+"F0.imprint","IMPRINT",FACE,{"disambiguationData":[TD([[makeQuery(id+"F0.imprint","IMPRINT",EDGE,{"derivedFrom":sQuery(id+"F0.wireOp",EDGE,"E43")}),1.0]])]});
            var Q21;
            Q21=makeQuery(id+"F0.imprint","IMPRINT",FACE,{"disambiguationData":[TD([[makeQuery(id+"F0.imprint","IMPRINT",EDGE,{"derivedFrom":sQuery(id+"F0.wireOp",EDGE,"E47")}),-1.0]])]});
            var Q22;
            Q22=makeQuery(id+"F0.imprint","IMPRINT",FACE,{"disambiguationData":[TD([[makeQuery(id+"F0.imprint","IMPRINT",EDGE,{"derivedFrom":sQuery(id+"F0.wireOp",EDGE,"E47")}),1.0]])]});
            var Q23;
            Q23=makeQuery(id+"F0.imprint","IMPRINT",FACE,{"disambiguationData":[TD([[makeQuery(id+"F0.imprint","IMPRINT",EDGE,{"derivedFrom":sQuery(id+"F0.wireOp",EDGE,"E45")}),-1.0]])]});
            var Q24;
            Q24=makeQuery(id+"F0.imprint","IMPRINT",FACE,{"disambiguationData":[TD([[makeQuery(id+"F0.imprint","IMPRINT",EDGE,{"derivedFrom":sQuery(id+"F0.wireOp",EDGE,"E45")}),1.0]])]});
            var Q25;
            Q25=makeQuery(id+"F0.imprint","IMPRINT",FACE,{"disambiguationData":[TD([[makeQuery(id+"F0.imprint","IMPRINT",EDGE,{"derivedFrom":sQuery(id+"F0.wireOp",EDGE,"E41")}),-1.0]])]});
            var Q26;
            Q26=makeQuery(id+"F0.imprint","IMPRINT",FACE,{"disambiguationData":[TD([[makeQuery(id+"F0.imprint","IMPRINT",EDGE,{"derivedFrom":sQuery(id+"F0.wireOp",EDGE,"E41")}),1.0]])]});
            var Q27;
            Q27=makeQuery(id+"F0.imprint","IMPRINT",FACE,{"disambiguationData":[TD([[makeQuery(id+"F0.imprint","IMPRINT",EDGE,{"derivedFrom":sQuery(id+"F0.wireOp",EDGE,"E37")}),-1.0]])]});
            var Q28;
            Q28=makeQuery(id+"F0.imprint","IMPRINT",FACE,{"disambiguationData":[TD([[makeQuery(id+"F0.imprint","IMPRINT",EDGE,{"derivedFrom":sQuery(id+"F0.wireOp",EDGE,"E37")}),1.0]])]});
            var Q29;
            Q29=makeQuery(id+"F0.imprint","IMPRINT",FACE,{"disambiguationData":[TD([[makeQuery(id+"F0.imprint","IMPRINT",EDGE,{"derivedFrom":sQuery(id+"F0.wireOp",EDGE,"E39")}),-1.0]])]});
            var Q30;
            Q30=makeQuery(id+"F0.imprint","IMPRINT",FACE,{"disambiguationData":[TD([[makeQuery(id+"F0.imprint","IMPRINT",EDGE,{"derivedFrom":sQuery(id+"F0.wireOp",EDGE,"E39")}),1.0]])]});
            var Q31;
            Q31=makeQuery(id+"F0.imprint","IMPRINT",FACE,{"disambiguationData":[TD([[makeQuery(id+"F0.imprint","IMPRINT",EDGE,{"derivedFrom":sQuery(id+"F0.wireOp",EDGE,"E26")}),-1.0]])]});
            var Q32;
            Q32=makeQuery(id+"F0.imprint","IMPRINT",FACE,{"disambiguationData":[TD([[makeQuery(id+"F0.imprint","IMPRINT",EDGE,{"derivedFrom":sQuery(id+"F0.wireOp",EDGE,"E26")}),1.0]])]});
            var Q33;
            Q33=makeQuery(id+"F0.imprint","IMPRINT",FACE,{"disambiguationData":[TD([[makeQuery(id+"F0.imprint","IMPRINT",EDGE,{"derivedFrom":sQuery(id+"F0.wireOp",EDGE,"E31")}),1.0]])]});
            var Q34;
            Q34=makeQuery(id+"F0.imprint","IMPRINT",FACE,{"disambiguationData":[TD([[makeQuery(id+"F0.imprint","IMPRINT",EDGE,{"derivedFrom":sQuery(id+"F0.wireOp",EDGE,"E31")}),-1.0]])]});
            var Q35;
            Q35=makeQuery(id+"F0.imprint","IMPRINT",FACE,{"disambiguationData":[TD([[makeQuery(id+"F0.imprint","IMPRINT",EDGE,{"derivedFrom":sQuery(id+"F0.wireOp",EDGE,"E33")}),1.0]])]});
            var Q36;
            Q36=makeQuery(id+"F0.imprint","IMPRINT",FACE,{"disambiguationData":[TD([[makeQuery(id+"F0.imprint","IMPRINT",EDGE,{"derivedFrom":sQuery(id+"F0.wireOp",EDGE,"E33")}),-1.0]])]});
            var Q37;
            Q37=makeQuery(id+"F0.imprint","IMPRINT",FACE,{"disambiguationData":[TD([[makeQuery(id+"F0.imprint","IMPRINT",EDGE,{"derivedFrom":sQuery(id+"F0.wireOp",EDGE,"E35")}),-1.0]])]});
            var Q38;
            Q38=makeQuery(id+"F0.imprint","IMPRINT",FACE,{"disambiguationData":[TD([[makeQuery(id+"F0.imprint","IMPRINT",EDGE,{"derivedFrom":sQuery(id+"F0.wireOp",EDGE,"E35")}),1.0]])]});
            var Q39;
            Q39=makeQuery(id+"F0.imprint","IMPRINT",FACE,{"disambiguationData":[TD([[makeQuery(id+"F0.imprint","IMPRINT",EDGE,{"derivedFrom":sQuery(id+"F0.wireOp",EDGE,"E29")}),-1.0]])]});
            var Q40;
            Q40=makeQuery(id+"F0.imprint","IMPRINT",FACE,{"disambiguationData":[TD([[makeQuery(id+"F0.imprint","IMPRINT",EDGE,{"derivedFrom":sQuery(id+"F0.wireOp",EDGE,"E29")}),1.0]])]});
            var Q41;
            Q41=makeQuery(id+"F0.imprint","IMPRINT",FACE,{"disambiguationData":[TD([[makeQuery(id+"F0.imprint","IMPRINT",EDGE,{"derivedFrom":sQuery(id+"F0.wireOp",EDGE,"E25")}),-1.0]])]});
            var Q42;
            Q42=makeQuery(id+"F0.imprint","IMPRINT",FACE,{"disambiguationData":[TD([[makeQuery(id+"F0.imprint","IMPRINT",EDGE,{"derivedFrom":sQuery(id+"F0.wireOp",EDGE,"E25")}),1.0]])]});
            var Q43;
            Q43=makeQuery(id+"F0.imprint","IMPRINT",FACE,{"disambiguationData":[TD([[makeQuery(id+"F0.imprint","IMPRINT",EDGE,{"derivedFrom":sQuery(id+"F0.wireOp",EDGE,"E17")}),-1.0]])]});
            var Q44;
            Q44=makeQuery(id+"F0.imprint","IMPRINT",FACE,{"disambiguationData":[TD([[makeQuery(id+"F0.imprint","IMPRINT",EDGE,{"derivedFrom":sQuery(id+"F0.wireOp",EDGE,"E17")}),1.0]])]});
            var Q45;
            Q45=makeQuery(id+"F0.imprint","IMPRINT",FACE,{"disambiguationData":[TD([[makeQuery(id+"F0.imprint","IMPRINT",EDGE,{"derivedFrom":sQuery(id+"F0.wireOp",EDGE,"E9")}),1.0]])]});
            var Q46;
            Q46=makeQuery(id+"F0.imprint","IMPRINT",FACE,{"disambiguationData":[TD([[makeQuery(id+"F0.imprint","IMPRINT",EDGE,{"derivedFrom":sQuery(id+"F0.wireOp",EDGE,"E10")}),1.0]])]});
            var Q47;
            Q47=makeQuery(id+"F0.imprint","IMPRINT",FACE,{"disambiguationData":[TD([[makeQuery(id+"F0.imprint","IMPRINT",EDGE,{"derivedFrom":sQuery(id+"F0.wireOp",EDGE,"E7")}),-1.0]])]});
            var Q48;
            Q48=makeQuery(id+"F0.imprint","IMPRINT",FACE,{"disambiguationData":[TD([[makeQuery(id+"F0.imprint","IMPRINT",EDGE,{"derivedFrom":sQuery(id+"F0.wireOp",EDGE,"E7")}),1.0]])]});
            var Q49;
            Q49=makeQuery(id+"F0.imprint","IMPRINT",FACE,{"disambiguationData":[TD([[makeQuery(id+"F0.imprint","IMPRINT",EDGE,{"derivedFrom":sQuery(id+"F0.wireOp",EDGE,"E11")}),-1.0]])]});
            var Q50;
            Q50=makeQuery(id+"F0.imprint","IMPRINT",FACE,{"disambiguationData":[TD([[makeQuery(id+"F0.imprint","IMPRINT",EDGE,{"derivedFrom":sQuery(id+"F0.wireOp",EDGE,"E11")}),1.0]])]});
            var Q51;
            Q51=makeQuery(id+"F0.imprint","IMPRINT",FACE,{"disambiguationData":[TD([[makeQuery(id+"F0.imprint","IMPRINT",EDGE,{"derivedFrom":sQuery(id+"F0.wireOp",EDGE,"E13")}),-1.0]])]});
            var Q52;
            Q52=makeQuery(id+"F0.imprint","IMPRINT",FACE,{"disambiguationData":[TD([[makeQuery(id+"F0.imprint","IMPRINT",EDGE,{"derivedFrom":sQuery(id+"F0.wireOp",EDGE,"E13")}),1.0]])]});
            var Q53;
            Q53=makeQuery(id+"F0.imprint","IMPRINT",FACE,{"disambiguationData":[TD([[makeQuery(id+"F0.imprint","IMPRINT",EDGE,{"derivedFrom":sQuery(id+"F0.wireOp",EDGE,"E23")}),-1.0]])]});
            var Q54;
            Q54=makeQuery(id+"F0.imprint","IMPRINT",FACE,{"disambiguationData":[TD([[makeQuery(id+"F0.imprint","IMPRINT",EDGE,{"derivedFrom":sQuery(id+"F0.wireOp",EDGE,"E23")}),1.0]])]});
            var Q55;
            Q55=makeQuery(id+"F0.imprint","IMPRINT",FACE,{"disambiguationData":[TD([[makeQuery(id+"F0.imprint","IMPRINT",EDGE,{"derivedFrom":sQuery(id+"F0.wireOp",EDGE,"E15")}),-1.0]])]});
            var Q56;
            Q56=makeQuery(id+"F0.imprint","IMPRINT",FACE,{"disambiguationData":[TD([[makeQuery(id+"F0.imprint","IMPRINT",EDGE,{"derivedFrom":sQuery(id+"F0.wireOp",EDGE,"E15")}),1.0]])]});
            var Q57;
            Q57=makeQuery(id+"F0.imprint","IMPRINT",FACE,{"disambiguationData":[TD([[makeQuery(id+"F0.imprint","IMPRINT",EDGE,{"derivedFrom":sQuery(id+"F0.wireOp",EDGE,"E19")}),-1.0]])]});
            var Q58;
            Q58=makeQuery(id+"F0.imprint","IMPRINT",FACE,{"disambiguationData":[TD([[makeQuery(id+"F0.imprint","IMPRINT",EDGE,{"derivedFrom":sQuery(id+"F0.wireOp",EDGE,"E19")}),1.0]])]});
            var Q59;
            Q59=makeQuery(id+"F0.imprint","IMPRINT",FACE,{"disambiguationData":[TD([[makeQuery(id+"F0.imprint","IMPRINT",EDGE,{"derivedFrom":sQuery(id+"F0.wireOp",EDGE,"E21")}),-1.0]])]});
            var Q60;
            Q60=makeQuery(id+"F0.imprint","IMPRINT",FACE,{"disambiguationData":[TD([[makeQuery(id+"F0.imprint","IMPRINT",EDGE,{"derivedFrom":sQuery(id+"F0.wireOp",EDGE,"E21")}),1.0]])]});
            var Q61;
            Q61=makeQuery(id+"F0.imprint","IMPRINT",FACE,{"disambiguationData":[TD([[makeQuery(id+"F0.imprint","IMPRINT",EDGE,{"derivedFrom":sQuery(id+"F0.wireOp",EDGE,"E96.bottom")}),-1.0]])]});
            var Q62;
            Q62=makeQuery(id+"F0.imprint","IMPRINT",FACE,{"disambiguationData":[TD([[makeQuery(id+"F0.imprint","IMPRINT",EDGE,{"derivedFrom":sQuery(id+"F0.wireOp",EDGE,"E97.bottom")}),-1.0]])]});
            var Q63;
            Q63=makeQuery(id+"F0.imprint","IMPRINT",FACE,{"disambiguationData":[TD([[makeQuery(id+"F0.imprint","IMPRINT",EDGE,{"derivedFrom":sQuery(id+"F0.wireOp",EDGE,"E98.bottom")}),-1.0]])]});
            var Q64;
            Q64=makeQuery(id+"F0.imprint","IMPRINT",FACE,{"disambiguationData":[TD([[makeQuery(id+"F0.imprint","IMPRINT",EDGE,{"derivedFrom":sQuery(id+"F0.wireOp",EDGE,"E95.bottom")}),-1.0]])]});
            var Q65;
            Q65=makeQuery(id+"F0.imprint","IMPRINT",FACE,{"disambiguationData":[TD([[makeQuery(id+"F0.imprint","IMPRINT",EDGE,{"derivedFrom":sQuery(id+"F0.wireOp",EDGE,"E94.bottom")}),-1.0]])]});
            extrude(context, id + "F2", {"entities" : qUnion([Q0, Q1, Q2, Q3, Q4, Q5, Q6, Q7, Q8, Q9, Q10, Q11, Q12, Q13, Q14, Q15, Q16, Q17, Q18, Q19, Q20, Q21, Q22, Q23, Q24, Q25, Q26, Q27, Q28, Q29, Q30, Q31, Q32, Q33, Q34, Q35, Q36, Q37, Q38, Q39, Q40, Q41, Q42, Q43, Q44, Q45, Q46, Q47, Q48, Q49, Q50, Q51, Q52, Q53, Q54, Q55, Q56, Q57, Q58, Q59, Q60, Q61, Q62, Q63, Q64, Q65]), "depth" : 25 * mm});
        }
        {
            var Q0;
            Q0=makeQuery(id+"F1.opExtrude","CAP_EDGE",EDGE,{"disambiguationData":[OSD([sQuery(id+"F0.wireOp",EDGE,"E37")])],"isStart":false});
            var Q1;
            Q1=makeQuery(id+"F1.opExtrude","CAP_EDGE",EDGE,{"disambiguationData":[OSD([sQuery(id+"F0.wireOp",EDGE,"E39")])],"isStart":false});
            var Q2;
            Q2=makeQuery(id+"F1.opExtrude","CAP_EDGE",EDGE,{"disambiguationData":[OSD([sQuery(id+"F0.wireOp",EDGE,"E26")])],"isStart":false});
            var Q3;
            Q3=makeQuery(id+"F1.opExtrude","CAP_EDGE",EDGE,{"disambiguationData":[OSD([sQuery(id+"F0.wireOp",EDGE,"E25")])],"isStart":false});
            var Q4;
            Q4=makeQuery(id+"F1.opExtrude","CAP_EDGE",EDGE,{"disambiguationData":[OSD([sQuery(id+"F0.wireOp",EDGE,"E21")])],"isStart":false});
            var Q5;
            Q5=makeQuery(id+"F1.opExtrude","CAP_EDGE",EDGE,{"disambiguationData":[OSD([sQuery(id+"F0.wireOp",EDGE,"E19")])],"isStart":false});
            var Q6;
            Q6=makeQuery(id+"F1.opExtrude","CAP_EDGE",EDGE,{"disambiguationData":[OSD([sQuery(id+"F0.wireOp",EDGE,"E17")])],"isStart":false});
            var Q7;
            Q7=makeQuery(id+"F1.opExtrude","CAP_EDGE",EDGE,{"disambiguationData":[OSD([sQuery(id+"F0.wireOp",EDGE,"E10")])],"isStart":false});
            var Q8;
            Q8=makeQuery(id+"F1.opExtrude","CAP_EDGE",EDGE,{"disambiguationData":[OSD([sQuery(id+"F0.wireOp",EDGE,"E15")])],"isStart":false});
            var Q9;
            Q9=makeQuery(id+"F1.opExtrude","CAP_EDGE",EDGE,{"disambiguationData":[OSD([sQuery(id+"F0.wireOp",EDGE,"E23")])],"isStart":false});
            var Q10;
            Q10=makeQuery(id+"F1.opExtrude","CAP_EDGE",EDGE,{"disambiguationData":[OSD([sQuery(id+"F0.wireOp",EDGE,"E11")])],"isStart":false});
            var Q11;
            Q11=makeQuery(id+"F1.opExtrude","CAP_EDGE",EDGE,{"disambiguationData":[OSD([sQuery(id+"F0.wireOp",EDGE,"E7")])],"isStart":false});
            var Q12;
            Q12=makeQuery(id+"F1.opExtrude","CAP_EDGE",EDGE,{"disambiguationData":[OSD([sQuery(id+"F0.wireOp",EDGE,"E13")])],"isStart":false});
            var Q13;
            Q13=makeQuery(id+"F1.opExtrude","CAP_FACE",FACE,{"disambiguationData":[OSD([sQuery(id+"F0.wireOp",EDGE,"E35")])],"isStart":false});
            var Q14;
            Q14=makeQuery(id+"F1.opExtrude","CAP_EDGE",EDGE,{"disambiguationData":[OSD([sQuery(id+"F0.wireOp",EDGE,"E29")])],"isStart":false});
            var Q15;
            Q15=makeQuery(id+"F1.opExtrude","CAP_EDGE",EDGE,{"disambiguationData":[OSD([sQuery(id+"F0.wireOp",EDGE,"E31")])],"isStart":false});
            var Q16;
            Q16=makeQuery(id+"F1.opExtrude","CAP_EDGE",EDGE,{"disambiguationData":[OSD([sQuery(id+"F0.wireOp",EDGE,"E33")])],"isStart":false});
            var Q17;
            Q17=makeQuery(id+"F1.opExtrude","CAP_EDGE",EDGE,{"disambiguationData":[OSD([sQuery(id+"F0.wireOp",EDGE,"E45")])],"isStart":false});
            var Q18;
            Q18=makeQuery(id+"F1.opExtrude","CAP_EDGE",EDGE,{"disambiguationData":[OSD([sQuery(id+"F0.wireOp",EDGE,"E41")])],"isStart":false});
            var Q19;
            Q19=makeQuery(id+"F1.opExtrude","CAP_EDGE",EDGE,{"disambiguationData":[OSD([sQuery(id+"F0.wireOp",EDGE,"E43")])],"isStart":false});
            var Q20;
            Q20=makeQuery(id+"F1.opExtrude","CAP_EDGE",EDGE,{"disambiguationData":[OSD([sQuery(id+"F0.wireOp",EDGE,"E47")])],"isStart":false});
            var Q21;
            Q21=makeQuery(id+"F1.opExtrude","CAP_EDGE",EDGE,{"disambiguationData":[OSD([sQuery(id+"F0.wireOp",EDGE,"E51")])],"isStart":false});
            var Q22;
            Q22=makeQuery(id+"F1.opExtrude","CAP_EDGE",EDGE,{"disambiguationData":[OSD([sQuery(id+"F0.wireOp",EDGE,"E49")])],"isStart":false});
            var Q23;
            Q23=makeQuery(id+"F1.opExtrude","CAP_EDGE",EDGE,{"disambiguationData":[OSD([sQuery(id+"F0.wireOp",EDGE,"E57")])],"isStart":false});
            var Q24;
            Q24=makeQuery(id+"F1.opExtrude","CAP_EDGE",EDGE,{"disambiguationData":[OSD([sQuery(id+"F0.wireOp",EDGE,"E55")])],"isStart":false});
            var Q25;
            Q25=makeQuery(id+"F1.opExtrude","CAP_EDGE",EDGE,{"disambiguationData":[OSD([sQuery(id+"F0.wireOp",EDGE,"E53")])],"isStart":false});
            var Q26;
            Q26=makeQuery(id+"F1.opExtrude","CAP_EDGE",EDGE,{"disambiguationData":[OSD([sQuery(id+"F0.wireOp",EDGE,"E59")])],"isStart":false});
            var Q27;
            Q27=makeQuery(id+"F1.opExtrude","CAP_EDGE",EDGE,{"disambiguationData":[OSD([sQuery(id+"F0.wireOp",EDGE,"E63")])],"isStart":false});
            var Q28;
            Q28=makeQuery(id+"F1.opExtrude","CAP_EDGE",EDGE,{"disambiguationData":[OSD([sQuery(id+"F0.wireOp",EDGE,"E3")])],"isStart":false});
            fillet(context, id + "F3", {"entities" : qUnion([Q0, Q1, Q2, Q3, Q4, Q5, Q6, Q7, Q8, Q9, Q10, Q11, Q12, Q13, Q14, Q15, Q16, Q17, Q18, Q19, Q20, Q21, Q22, Q23, Q24, Q25, Q26, Q27, Q28]), "radius" : 63 * mm, "tangentPropagation" : true, "allowEdgeOverflow" : false});
        }
        {
            var Q0;
            Q0=makeQuery(id+"F1.opExtrude","CAP_EDGE",EDGE,{"disambiguationData":[OSD([sQuery(id+"F0.wireOp",EDGE,"E61")])],"isStart":false});
            fillet(context, id + "F4", {"entities" : qUnion([Q0]), "radius" : 61 * mm, "tangentPropagation" : true, "allowEdgeOverflow" : false});
        }
        {
            var Q0;
            Q0=makeQuery(id+"F0.imprint","IMPRINT",FACE,{"disambiguationData":[TD([[makeQuery(id+"F0.imprint","IMPRINT",EDGE,{"derivedFrom":sQuery(id+"F0.wireOp",EDGE,"E94.bottom")}),-1.0]])]});
            var Q1;
            Q1=makeQuery(id+"F0.imprint","IMPRINT",FACE,{"disambiguationData":[TD([[makeQuery(id+"F0.imprint","IMPRINT",EDGE,{"derivedFrom":sQuery(id+"F0.wireOp",EDGE,"E95.bottom")}),-1.0]])]});
            var Q2;
            Q2=makeQuery(id+"F0.imprint","IMPRINT",FACE,{"disambiguationData":[TD([[makeQuery(id+"F0.imprint","IMPRINT",EDGE,{"derivedFrom":sQuery(id+"F0.wireOp",EDGE,"E96.bottom")}),-1.0]])]});
            var Q3;
            Q3=makeQuery(id+"F0.imprint","IMPRINT",FACE,{"disambiguationData":[TD([[makeQuery(id+"F0.imprint","IMPRINT",EDGE,{"derivedFrom":sQuery(id+"F0.wireOp",EDGE,"E97.bottom")}),-1.0]])]});
            var Q4;
            Q4=makeQuery(id+"F0.imprint","IMPRINT",FACE,{"disambiguationData":[TD([[makeQuery(id+"F0.imprint","IMPRINT",EDGE,{"derivedFrom":sQuery(id+"F0.wireOp",EDGE,"E98.bottom")}),-1.0]])]});
            extrude(context, id + "F5", {"entities" : qUnion([Q0, Q1, Q2, Q3, Q4]), "operationType" : NewBodyOperationType.ADD, "oppositeDirection" : true, "depth" : 90 * mm});
        }
        {
            var Q0;
            Q0=makeQuery(id+"F5.opExtrude","SWEPT_EDGE",EDGE,{"disambiguationData":[OSD([sQuery(id+"F0.wireOp",EDGE,"E94.top"),sQuery(id+"F0.wireOp",EDGE,"E94.left")])]});
            var Q1;
            Q1=makeQuery(id+"F5.opExtrude","SWEPT_EDGE",EDGE,{"disambiguationData":[OSD([sQuery(id+"F0.wireOp",EDGE,"E94.top"),sQuery(id+"F0.wireOp",EDGE,"E94.right")])]});
            var Q2;
            Q2=makeQuery(id+"F5.opExtrude","SWEPT_EDGE",EDGE,{"disambiguationData":[OSD([sQuery(id+"F0.wireOp",EDGE,"E95.top"),sQuery(id+"F0.wireOp",EDGE,"E95.left")])]});
            var Q3;
            Q3=makeQuery(id+"F5.opExtrude","SWEPT_EDGE",EDGE,{"disambiguationData":[OSD([sQuery(id+"F0.wireOp",EDGE,"E95.top"),sQuery(id+"F0.wireOp",EDGE,"E95.right")])]});
            var Q4;
            Q4=makeQuery(id+"F5.opExtrude","CAP_EDGE",EDGE,{"disambiguationData":[OSD([sQuery(id+"F0.wireOp",EDGE,"E94.top")])],"isStart":false});
            var Q5;
            Q5=makeQuery(id+"F5.opExtrude","CAP_EDGE",EDGE,{"disambiguationData":[OSD([sQuery(id+"F0.wireOp",EDGE,"E95.top")])],"isStart":false});
            var Q6;
            Q6=makeQuery(id+"F5.opExtrude","CAP_EDGE",EDGE,{"disambiguationData":[OSD([sQuery(id+"F0.wireOp",EDGE,"E96.top")])],"isStart":false});
            var Q7;
            Q7=makeQuery(id+"F5.opExtrude","SWEPT_EDGE",EDGE,{"disambiguationData":[OSD([sQuery(id+"F0.wireOp",EDGE,"E96.top"),sQuery(id+"F0.wireOp",EDGE,"E96.right")])]});
            var Q8;
            Q8=makeQuery(id+"F5.opExtrude","SWEPT_EDGE",EDGE,{"disambiguationData":[OSD([sQuery(id+"F0.wireOp",EDGE,"E96.top"),sQuery(id+"F0.wireOp",EDGE,"E96.left")])]});
            var Q9;
            Q9=makeQuery(id+"F5.opExtrude","CAP_EDGE",EDGE,{"disambiguationData":[OSD([sQuery(id+"F0.wireOp",EDGE,"E97.top")])],"isStart":false});
            var Q10;
            Q10=makeQuery(id+"F5.opExtrude","SWEPT_EDGE",EDGE,{"disambiguationData":[OSD([sQuery(id+"F0.wireOp",EDGE,"E97.top"),sQuery(id+"F0.wireOp",EDGE,"E97.right")])]});
            var Q11;
            Q11=makeQuery(id+"F5.opExtrude","SWEPT_EDGE",EDGE,{"disambiguationData":[OSD([sQuery(id+"F0.wireOp",EDGE,"E97.top"),sQuery(id+"F0.wireOp",EDGE,"E97.left")])]});
            var Q12;
            Q12=makeQuery(id+"F5.opExtrude","CAP_EDGE",EDGE,{"disambiguationData":[OSD([sQuery(id+"F0.wireOp",EDGE,"E94.right")])],"isStart":false});
            var Q13;
            Q13=makeQuery(id+"F5.opExtrude","CAP_EDGE",EDGE,{"disambiguationData":[OSD([sQuery(id+"F0.wireOp",EDGE,"E94.left")])],"isStart":false});
            var Q14;
            Q14=makeQuery(id+"F5.opExtrude","CAP_EDGE",EDGE,{"disambiguationData":[OSD([sQuery(id+"F0.wireOp",EDGE,"E95.left")])],"isStart":false});
            var Q15;
            Q15=makeQuery(id+"F5.opExtrude","CAP_EDGE",EDGE,{"disambiguationData":[OSD([sQuery(id+"F0.wireOp",EDGE,"E95.right")])],"isStart":false});
            var Q16;
            Q16=makeQuery(id+"F5.opExtrude","CAP_EDGE",EDGE,{"disambiguationData":[OSD([sQuery(id+"F0.wireOp",EDGE,"E96.left")])],"isStart":false});
            var Q17;
            Q17=makeQuery(id+"F5.opExtrude","CAP_EDGE",EDGE,{"disambiguationData":[OSD([sQuery(id+"F0.wireOp",EDGE,"E96.right")])],"isStart":false});
            var Q18;
            Q18=makeQuery(id+"F5.opExtrude","CAP_EDGE",EDGE,{"disambiguationData":[OSD([sQuery(id+"F0.wireOp",EDGE,"E97.left")])],"isStart":false});
            var Q19;
            Q19=makeQuery(id+"F5.opExtrude","SWEPT_EDGE",EDGE,{"disambiguationData":[OSD([sQuery(id+"F0.wireOp",EDGE,"E98.top"),sQuery(id+"F0.wireOp",EDGE,"E98.right")])]});
            var Q20;
            Q20=makeQuery(id+"F5.opExtrude","CAP_EDGE",EDGE,{"disambiguationData":[OSD([sQuery(id+"F0.wireOp",EDGE,"E98.top")])],"isStart":false});
            var Q21;
            Q21=makeQuery(id+"F5.opExtrude","SWEPT_EDGE",EDGE,{"disambiguationData":[OSD([sQuery(id+"F0.wireOp",EDGE,"E98.top"),sQuery(id+"F0.wireOp",EDGE,"E98.left")])]});
            var Q22;
            Q22=makeQuery(id+"F5.opExtrude","CAP_EDGE",EDGE,{"disambiguationData":[OSD([sQuery(id+"F0.wireOp",EDGE,"E98.left")])],"isStart":false});
            var Q23;
            Q23=makeQuery(id+"F5.opExtrude","CAP_EDGE",EDGE,{"disambiguationData":[OSD([sQuery(id+"F0.wireOp",EDGE,"E98.right")])],"isStart":false});
            var Q24;
            Q24=makeQuery(id+"F5.opExtrude","SWEPT_EDGE",EDGE,{"disambiguationData":[OSD([sQuery(id+"F0.wireOp",EDGE,"E98.bottom"),sQuery(id+"F0.wireOp",EDGE,"E98.right")])]});
            var Q25;
            Q25=makeQuery(id+"F5.opExtrude","CAP_EDGE",EDGE,{"disambiguationData":[OSD([sQuery(id+"F0.wireOp",EDGE,"E97.bottom")])],"isStart":false});
            var Q26;
            Q26=makeQuery(id+"F5.opExtrude","CAP_EDGE",EDGE,{"disambiguationData":[OSD([sQuery(id+"F0.wireOp",EDGE,"E97.right")])],"isStart":false});
            var Q27;
            Q27=makeQuery(id+"F5.opExtrude","SWEPT_EDGE",EDGE,{"disambiguationData":[OSD([sQuery(id+"F0.wireOp",EDGE,"E97.bottom"),sQuery(id+"F0.wireOp",EDGE,"E97.right")])]});
            var Q28;
            Q28=makeQuery(id+"F5.opExtrude","SWEPT_EDGE",EDGE,{"disambiguationData":[OSD([sQuery(id+"F0.wireOp",EDGE,"E97.bottom"),sQuery(id+"F0.wireOp",EDGE,"E97.left")])]});
            var Q29;
            Q29=makeQuery(id+"F5.opExtrude","SWEPT_EDGE",EDGE,{"disambiguationData":[OSD([sQuery(id+"F0.wireOp",EDGE,"E96.bottom"),sQuery(id+"F0.wireOp",EDGE,"E96.right")])]});
            var Q30;
            Q30=makeQuery(id+"F5.opExtrude","SWEPT_EDGE",EDGE,{"disambiguationData":[OSD([sQuery(id+"F0.wireOp",EDGE,"E38"),sQuery(id+"F0.wireOp",EDGE,"E96.bottom"),sQuery(id+"F0.wireOp",EDGE,"E96.left")])]});
            var Q31;
            Q31=makeQuery(id+"F5.opExtrude","SWEPT_EDGE",EDGE,{"disambiguationData":[OSD([sQuery(id+"F0.wireOp",EDGE,"E95.bottom"),sQuery(id+"F0.wireOp",EDGE,"E95.right")])]});
            var Q32;
            Q32=makeQuery(id+"F5.opExtrude","SWEPT_EDGE",EDGE,{"disambiguationData":[OSD([sQuery(id+"F0.wireOp",EDGE,"E95.bottom"),sQuery(id+"F0.wireOp",EDGE,"E95.left")])]});
            var Q33;
            Q33=makeQuery(id+"F5.opExtrude","SWEPT_EDGE",EDGE,{"disambiguationData":[OSD([sQuery(id+"F0.wireOp",EDGE,"E98.bottom"),sQuery(id+"F0.wireOp",EDGE,"E98.left")])]});
            fillet(context, id + "F6", {"entities" : qUnion([Q0, Q1, Q2, Q3, Q4, Q5, Q6, Q7, Q8, Q9, Q10, Q11, Q12, Q13, Q14, Q15, Q16, Q17, Q18, Q19, Q20, Q21, Q22, Q23, Q24, Q25, Q26, Q27, Q28, Q29, Q30, Q31, Q32, Q33]), "radius" : 20 * mm, "tangentPropagation" : true, "allowEdgeOverflow" : false});
        }
    });
